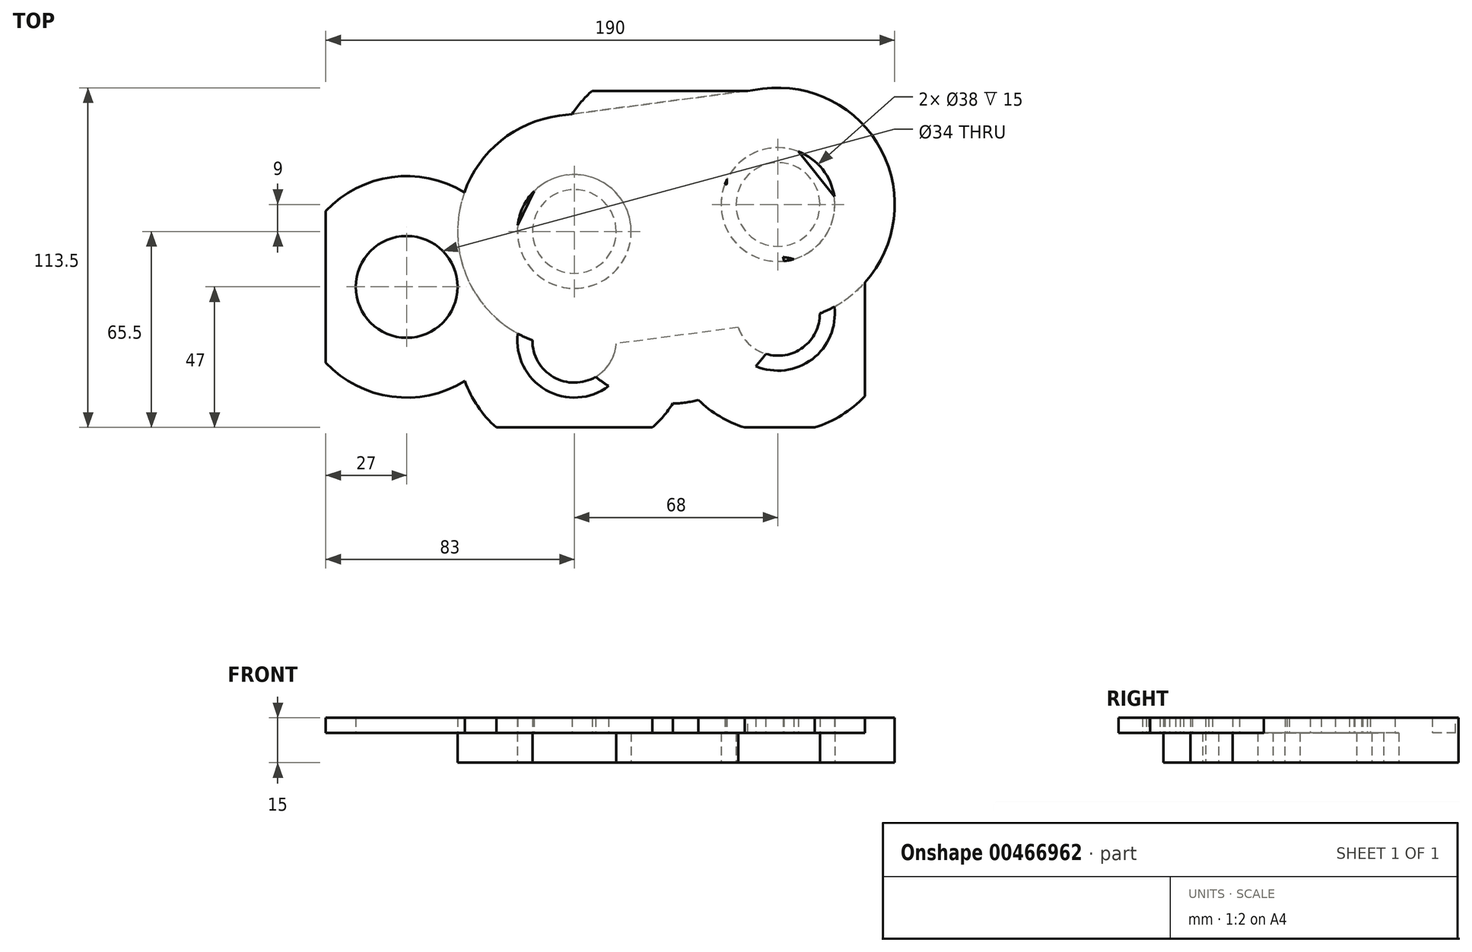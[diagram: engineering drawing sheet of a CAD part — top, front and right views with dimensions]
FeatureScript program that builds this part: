
annotation { "Feature Type Name" : "Feature", "Feature Type Description" : "" }
export const myFeature = defineFeature(function(context is Context, id is Id, definition is map)
    precondition{}
    {
        {
            var Q0;
            Q0=qCreatedBy(makeId("Top.planeOp"),FACE);
            var sketch = newSketch(context, id + "F0", { "sketchPlane" : qUnion([Q0])});
            skCircle(sketch, "E0", {"center": v(0, 0) * mm, "radius": 12 * mm, "construction": true});
            skCircle(sketch, "E1", {"center": v(56, 18.5) * mm, "radius": 14 * mm, "construction": true});
            skCircle(sketch, "E2", {"center": v(88, 36.5) * mm, "radius": 14 * mm, "construction": true});
            skCircle(sketch, "E3", {"center": v(124, 27.5) * mm, "radius": 14 * mm, "construction": true});
            skCircle(sketch, "E4", {"center": v(56, -18) * mm, "radius": 14 * mm, "construction": true});
            skCircle(sketch, "E5", {"center": v(88, 0) * mm, "radius": 14 * mm, "construction": true});
            skCircle(sketch, "E6", {"center": v(124, -9) * mm, "radius": 14 * mm, "construction": true});
            skSolve(sketch);
        }
        {
            var Q0;
            Q0=qCreatedBy(makeId("Top.planeOp"),FACE);
            var sketch = newSketch(context, id + "F1", { "sketchPlane" : qUnion([Q0])});
            skCircle(sketch, "E7.0", {"center": v(0, 0) * mm, "radius": 17 * mm});
            skCircle(sketch, "E8.0", {"center": v(56, -18) * mm, "radius": 19 * mm});
            skCircle(sketch, "E9.0", {"center": v(124, -9) * mm, "radius": 19 * mm});
            skCircle(sketch, "E10.0", {"center": v(88, 36.5) * mm, "radius": 19 * mm});
            skPoint(sketch, "E11.0", {"position": v(56, 18.5) * mm});
            skPoint(sketch, "E11.1", {"position": v(88, 0) * mm});
            skPoint(sketch, "E11.2", {"position": v(124, 27.5) * mm});
            skCircle(sketch, "E12", {"center": v(56, 18.5) * mm, "radius": 1.5 * mm});
            skCircle(sketch, "E13", {"center": v(88, 0) * mm, "radius": 1.5 * mm});
            skCircle(sketch, "E14", {"center": v(124, 27.5) * mm, "radius": 1.5 * mm});
            skArc(sketch, "E15.0", {"start": v(34.1, 14.36) * mm, "mid": v(6.52, 36.42) * mm, "end": v(-27, 25.3) * mm});
            skArc(sketch, "E16.0", {"start": v(19.41, -31.5) * mm, "mid": v(23.72, -39.9) * mm, "end": v(29.92, -47) * mm});
            skArc(sketch, "E17.0", {"start": v(118.57, 60.71) * mm, "mid": v(116.43, 63.2) * mm, "end": v(114.08, 65.5) * mm});
            skArc(sketch, "E18.trimOffspring", {"start": v(92.44, -31.9) * mm, "mid": v(101.38, -41.16) * mm, "end": v(112.86, -47) * mm});
            skLineSegment(sketch, "E19", {"start": v(118.57, 60.71) * mm, "end": v(153, 17.25) * mm});
            skLineSegment(sketch, "E20", {"start": v(34.1, 14.36) * mm, "end": v(52.85, 53.39) * mm});
            skLineSegment(sketch, "E21.bottom", {"start": v(61.92, 65.5) * mm, "end": v(114.08, 65.5) * mm});
            skLineSegment(sketch, "E21.top", {"start": v(29.92, -47) * mm, "end": v(82.08, -47) * mm});
            skLineSegment(sketch, "E21.left", {"start": v(-27, 25.3) * mm, "end": v(-27, -25.3) * mm});
            skLineSegment(sketch, "E21.right", {"start": v(153, 17.25) * mm, "end": v(153, -36.54) * mm});
            skArc(sketch, "E22.trimOffspring", {"start": v(-27, -25.3) * mm, "mid": v(-4.9, -36.67) * mm, "end": v(19.41, -31.5) * mm});
            skArc(sketch, "E23.trimOffspring", {"start": v(82.08, -47) * mm, "mid": v(88.15, -40.07) * mm, "end": v(92.44, -31.9) * mm});
            skLineSegment(sketch, "E24.trimOffspring", {"start": v(112.86, -47) * mm, "end": v(136.32, -47) * mm});
            skArc(sketch, "E25.trimOffspring", {"start": v(136.32, -47) * mm, "mid": v(145.33, -42.84) * mm, "end": v(153, -36.54) * mm});
            skArc(sketch, "E26.trimOffspring", {"start": v(61.92, 65.5) * mm, "mid": v(56.8, 59.89) * mm, "end": v(52.85, 53.39) * mm});
            skSolve(sketch);
        }
        {
            var Q0;
            Q0=makeQuery(id+"F1.imprint","IMPRINT",FACE,{"disambiguationData":[TD([[makeQuery(id+"F1.imprint","IMPRINT",EDGE,{"derivedFrom":sQuery(id+"F1.wireOp",EDGE,"E7.0")}),-1.0]])]});
            extrude(context, id + "F2", {"entities" : qUnion([Q0]), "depth" : 5 * mm});
        }
        {
            var Q0;
            Q0=makeQuery(id+"F2.opExtrude","CAP_FACE",FACE,{"disambiguationData":[OSD([sQuery(id+"F1.wireOp",EDGE,"E7.0"),sQuery(id+"F1.wireOp",EDGE,"E8.0"),sQuery(id+"F1.wireOp",EDGE,"E9.0"),sQuery(id+"F1.wireOp",EDGE,"E10.0"),sQuery(id+"F1.wireOp",EDGE,"E12"),sQuery(id+"F1.wireOp",EDGE,"E13"),sQuery(id+"F1.wireOp",EDGE,"E14"),sQuery(id+"F1.wireOp",EDGE,"E15.0"),sQuery(id+"F1.wireOp",EDGE,"E16.0"),sQuery(id+"F1.wireOp",EDGE,"E17.0"),sQuery(id+"F1.wireOp",EDGE,"E18.trimOffspring"),sQuery(id+"F1.wireOp",EDGE,"E19"),sQuery(id+"F1.wireOp",EDGE,"E20")])],"isStart":false});
            var sketch = newSketch(context, id + "F3", { "sketchPlane" : qUnion([Q0])});
            skCircle(sketch, "E27", {"center": v(56, 18.5) * mm, "radius": 3 * mm});
            skCircle(sketch, "E28", {"center": v(124, 27.5) * mm, "radius": 3 * mm});
            skCircle(sketch, "E29", {"center": v(88, 0) * mm, "radius": 3 * mm});
            skSolve(sketch);
        }
        {
            var Q0;
            Q0=makeQuery(id+"F3.imprint","IMPRINT",FACE,{"disambiguationData":[TD([[makeQuery(id+"F3.imprint","IMPRINT",EDGE,{"derivedFrom":sQuery(id+"F3.wireOp",EDGE,"E29")}),1.0]])]});
            var Q1;
            Q1=makeQuery(id+"F3.imprint","IMPRINT",FACE,{"disambiguationData":[TD([[makeQuery(id+"F3.imprint","IMPRINT",EDGE,{"derivedFrom":sQuery(id+"F3.wireOp",EDGE,"E27")}),1.0]])]});
            var Q2;
            Q2=makeQuery(id+"F3.imprint","IMPRINT",FACE,{"disambiguationData":[TD([[makeQuery(id+"F3.imprint","IMPRINT",EDGE,{"derivedFrom":sQuery(id+"F3.wireOp",EDGE,"E28")}),1.0]])]});
            var Q3;
            Q3=sQuery(id+"F3.wireOp",EDGE,"E27");
            var Q4;
            Q4=sQuery(id+"F3.wireOp",EDGE,"E29");
            var Q5;
            Q5=sQuery(id+"F3.wireOp",EDGE,"E28");
            extrude(context, id + "F4", {"entities" : qUnion([Q0, Q1, Q2]), "operationType" : NewBodyOperationType.REMOVE, "surfaceEntities" : qUnion([Q3, Q4, Q5]), "oppositeDirection" : true, "depth" : 3 * mm});
        }
        {
            var Q0;
            Q0=qCreatedBy(makeId("Top.planeOp"),FACE);
            var sketch = newSketch(context, id + "F5", { "sketchPlane" : qUnion([Q0])});
            skCircle(sketch, "E30.0", {"center": v(56, 18.5) * mm, "radius": 19 * mm});
            skCircle(sketch, "E31.0", {"center": v(124, 27.5) * mm, "radius": 19 * mm});
            skArc(sketch, "E32.0", {"start": v(50.88, 57.16) * mm, "mid": v(17.27, 23.08) * mm, "end": v(42, -17.9) * mm});
            skArc(sketch, "E33.0", {"start": v(138, -8.9) * mm, "mid": v(161.8, 37.13) * mm, "end": v(118.88, 66.16) * mm});
            skLineSegment(sketch, "E34", {"start": v(50.88, 57.16) * mm, "end": v(118.88, 66.16) * mm});
            skLineSegment(sketch, "E35", {"start": v(69.96, -19) * mm, "end": v(110.77, -13.6) * mm});
            skArc(sketch, "E36.0", {"start": v(42, -17.9) * mm, "mid": v(55.45, -31.99) * mm, "end": v(69.96, -19) * mm});
            skArc(sketch, "E36.1", {"start": v(110.77, -13.6) * mm, "mid": v(126.38, -22.8) * mm, "end": v(138, -8.9) * mm});
            skSolve(sketch);
        }
        {
            var Q0;
            Q0=makeQuery(id+"F5.imprint","IMPRINT",FACE,{"disambiguationData":[TD([[makeQuery(id+"F5.imprint","IMPRINT",EDGE,{"derivedFrom":sQuery(id+"F5.wireOp",EDGE,"E30.0")}),-1.0]])]});
            extrude(context, id + "F6", {"entities" : qUnion([Q0]), "depth" : 5 * mm});
        }
        {
            var Q0;
            Q0=makeQuery(id+"F6.opExtrude","CAP_FACE",FACE,{"disambiguationData":[OSD([sQuery(id+"F5.wireOp",EDGE,"E30.0"),sQuery(id+"F5.wireOp",EDGE,"E31.0"),sQuery(id+"F5.wireOp",EDGE,"E32.0"),sQuery(id+"F5.wireOp",EDGE,"E33.0"),sQuery(id+"F5.wireOp",EDGE,"E34"),sQuery(id+"F5.wireOp",EDGE,"E35"),sQuery(id+"F5.wireOp",EDGE,"E36.0"),sQuery(id+"F5.wireOp",EDGE,"E36.1")])],"isStart":true});
            var sketch = newSketch(context, id + "F7", { "sketchPlane" : qUnion([Q0])});
            skCircle(sketch, "E37.0", {"center": v(124, 9) * mm, "radius": 14 * mm});
            skCircle(sketch, "E37.1", {"center": v(88, -36.5) * mm, "radius": 14 * mm});
            skCircle(sketch, "E37.2", {"center": v(56, 18) * mm, "radius": 14 * mm});
            skSolve(sketch);
        }
        {
            var Q0;
            {var subQ0=sQuery(id+"F7.wireOp",EDGE,"E37.0");var subQ1=makeQuery(id+"F7.imprint","INTERSECT",VERTEX,{"derivedFrom":[makeQuery(id+"F6.opExtrude","CAP_EDGE",EDGE,{"disambiguationData":[OSD([sQuery(id+"F5.wireOp",EDGE,"E33.0")])],"isStart":true}),subQ0]});Q0=makeQuery(id+"F7.imprint","IMPRINT",FACE,{"disambiguationData":[TD([[makeQuery(id+"F7.imprint","IMPRINT",EDGE,{"disambiguationData":[TD([[subQ1,1.0]])],"derivedFrom":subQ0}),-1.0]])]});}
            var Q1;
            Q1=makeQuery(id+"F7.imprint","IMPRINT",FACE,{"disambiguationData":[TD([[makeQuery(id+"F7.imprint","IMPRINT",EDGE,{"derivedFrom":sQuery(id+"F7.wireOp",EDGE,"E37.1")}),-1.0]])]});
            var Q2;
            {var subQ0=sQuery(id+"F7.wireOp",EDGE,"E37.2");var subQ1=makeQuery(id+"F7.imprint","INTERSECT",VERTEX,{"derivedFrom":[makeQuery(id+"F6.opExtrude","CAP_EDGE",EDGE,{"disambiguationData":[OSD([sQuery(id+"F5.wireOp",EDGE,"E32.0")])],"isStart":true}),subQ0]});Q2=makeQuery(id+"F7.imprint","IMPRINT",FACE,{"disambiguationData":[TD([[makeQuery(id+"F7.imprint","IMPRINT",EDGE,{"disambiguationData":[TD([[subQ1,-1.0]])],"derivedFrom":subQ0}),-1.0]])]});}
            extrude(context, id + "F8", {"entities" : qUnion([Q0, Q1, Q2]), "operationType" : NewBodyOperationType.ADD, "depth" : 10 * mm});
        }
        {
            var Q0;
            Q0=qCreatedBy(makeId("Top.planeOp"),FACE);
            var sketch = newSketch(context, id + "F9", { "sketchPlane" : qUnion([Q0])});
            skCircle(sketch, "E38.0", {"center": v(88, 0) * mm, "radius": 19 * mm});
            skArc(sketch, "E39.0", {"start": v(49.48, 6.11) * mm, "mid": v(49, 0.23) * mm, "end": v(49.41, -5.65) * mm});
            skArc(sketch, "E40.0", {"start": v(102, 36.4) * mm, "mid": v(88, 50.5) * mm, "end": v(74, 36.4) * mm});
            skArc(sketch, "E40.1", {"start": v(49.41, -5.65) * mm, "mid": v(43.8, -24.86) * mm, "end": v(63.13, -30.05) * mm});
            skArc(sketch, "E40.2", {"start": v(119.93, -22.4) * mm, "mid": v(137.58, -12.4) * mm, "end": v(126.71, 4.73) * mm});
            skArc(sketch, "E40.3", {"start": v(124.58, 13.51) * mm, "mid": v(135.13, 36) * mm, "end": v(110.66, 31.74) * mm});
            skArc(sketch, "E40.4", {"start": v(63.48, 30.33) * mm, "mid": v(43.88, 25.5) * mm, "end": v(49.48, 6.11) * mm});
            skArc(sketch, "E41.trimOffspring", {"start": v(74, 36.4) * mm, "mid": v(68.5, 33.78) * mm, "end": v(63.48, 30.33) * mm});
            skArc(sketch, "E42.trimOffspring", {"start": v(110.66, 31.74) * mm, "mid": v(106.48, 34.35) * mm, "end": v(102, 36.4) * mm});
            skArc(sketch, "E43.trimOffspring", {"start": v(126.71, 4.73) * mm, "mid": v(125.9, 9.19) * mm, "end": v(124.58, 13.51) * mm});
            skArc(sketch, "E44.trimOffspring", {"start": v(63.13, -30.05) * mm, "mid": v(93.2, -38.65) * mm, "end": v(119.93, -22.4) * mm});
            skSolve(sketch);
        }
        {
            var Q0;
            Q0=makeQuery(id+"F9.imprint","IMPRINT",FACE,{"disambiguationData":[TD([[makeQuery(id+"F9.imprint","IMPRINT",EDGE,{"derivedFrom":sQuery(id+"F9.wireOp",EDGE,"E38.0")}),-1.0]])]});
            extrude(context, id + "F10", {"entities" : qUnion([Q0]), "depth" : 5 * mm});
        }
        {
            var Q0;
            Q0=makeQuery(id+"F10.opExtrude","CAP_FACE",FACE,{"disambiguationData":[OSD([sQuery(id+"F9.wireOp",EDGE,"E38.0"),sQuery(id+"F9.wireOp",EDGE,"E39.0"),sQuery(id+"F9.wireOp",EDGE,"E40.0"),sQuery(id+"F9.wireOp",EDGE,"E40.1"),sQuery(id+"F9.wireOp",EDGE,"E40.2"),sQuery(id+"F9.wireOp",EDGE,"E40.3"),sQuery(id+"F9.wireOp",EDGE,"E40.4"),sQuery(id+"F9.wireOp",EDGE,"E41.trimOffspring"),sQuery(id+"F9.wireOp",EDGE,"E42.trimOffspring"),sQuery(id+"F9.wireOp",EDGE,"E43.trimOffspring"),sQuery(id+"F9.wireOp",EDGE,"E44.trimOffspring")])],"isStart":true});
            var sketch = newSketch(context, id + "F11", { "sketchPlane" : qUnion([Q0])});
            skCircle(sketch, "E45.0", {"center": v(56, 18) * mm, "radius": 14 * mm});
            skCircle(sketch, "E45.1", {"center": v(124, 9) * mm, "radius": 14 * mm});
            skCircle(sketch, "E45.2", {"center": v(124, -27.5) * mm, "radius": 14 * mm});
            skCircle(sketch, "E45.3", {"center": v(88, -36.5) * mm, "radius": 14 * mm});
            skCircle(sketch, "E45.4", {"center": v(56, -18.5) * mm, "radius": 14 * mm});
            skSolve(sketch);
        }
        {
            var Q0;
            {var subQ0=sQuery(id+"F11.wireOp",EDGE,"E45.4");var subQ1=makeQuery(id+"F11.imprint","INTERSECT",VERTEX,{"derivedFrom":[makeQuery(id+"F10.opExtrude","CAP_EDGE",EDGE,{"disambiguationData":[OSD([sQuery(id+"F9.wireOp",EDGE,"E39.0")])],"isStart":true}),subQ0]});Q0=makeQuery(id+"F11.imprint","IMPRINT",FACE,{"disambiguationData":[TD([[makeQuery(id+"F11.imprint","IMPRINT",EDGE,{"disambiguationData":[TD([[subQ1,1.0]])],"derivedFrom":subQ0}),-1.0]])]});}
            var Q1;
            {var subQ0=sQuery(id+"F11.wireOp",EDGE,"E45.0");var subQ1=makeQuery(id+"F11.imprint","INTERSECT",VERTEX,{"derivedFrom":[makeQuery(id+"F10.opExtrude","CAP_EDGE",EDGE,{"disambiguationData":[OSD([sQuery(id+"F9.wireOp",EDGE,"E39.0")])],"isStart":true}),subQ0]});Q1=makeQuery(id+"F11.imprint","IMPRINT",FACE,{"disambiguationData":[TD([[makeQuery(id+"F11.imprint","IMPRINT",EDGE,{"disambiguationData":[TD([[subQ1,-1.0]])],"derivedFrom":subQ0}),-1.0]])]});}
            var Q2;
            {var subQ0=sQuery(id+"F11.wireOp",EDGE,"E45.3");var subQ1=makeQuery(id+"F11.imprint","INTERSECT",VERTEX,{"derivedFrom":[makeQuery(id+"F10.opExtrude","CAP_EDGE",EDGE,{"disambiguationData":[OSD([sQuery(id+"F9.wireOp",EDGE,"E42.trimOffspring")])],"isStart":true}),subQ0]});Q2=makeQuery(id+"F11.imprint","IMPRINT",FACE,{"disambiguationData":[TD([[makeQuery(id+"F11.imprint","IMPRINT",EDGE,{"disambiguationData":[TD([[subQ1,-1.0]])],"derivedFrom":subQ0}),-1.0]])]});}
            var Q3;
            {var subQ0=sQuery(id+"F11.wireOp",EDGE,"E45.2");var subQ1=makeQuery(id+"F11.imprint","INTERSECT",VERTEX,{"derivedFrom":[makeQuery(id+"F10.opExtrude","CAP_EDGE",EDGE,{"disambiguationData":[OSD([sQuery(id+"F9.wireOp",EDGE,"E43.trimOffspring")])],"isStart":true}),subQ0]});Q3=makeQuery(id+"F11.imprint","IMPRINT",FACE,{"disambiguationData":[TD([[makeQuery(id+"F11.imprint","IMPRINT",EDGE,{"disambiguationData":[TD([[subQ1,-1.0]])],"derivedFrom":subQ0}),-1.0]])]});}
            var Q4;
            {var subQ0=sQuery(id+"F11.wireOp",EDGE,"E45.1");var subQ1=makeQuery(id+"F11.imprint","INTERSECT",VERTEX,{"derivedFrom":[makeQuery(id+"F10.opExtrude","CAP_EDGE",EDGE,{"disambiguationData":[OSD([sQuery(id+"F9.wireOp",EDGE,"E44.trimOffspring")])],"isStart":true}),subQ0]});Q4=makeQuery(id+"F11.imprint","IMPRINT",FACE,{"disambiguationData":[TD([[makeQuery(id+"F11.imprint","IMPRINT",EDGE,{"disambiguationData":[TD([[subQ1,-1.0]])],"derivedFrom":subQ0}),-1.0]])]});}
            extrude(context, id + "F12", {"entities" : qUnion([Q0, Q1, Q2, Q3, Q4]), "operationType" : NewBodyOperationType.ADD, "depth" : 10 * mm});
        }
    });
